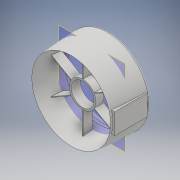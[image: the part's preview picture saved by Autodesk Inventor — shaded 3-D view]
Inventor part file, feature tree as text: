
AUTODESK INVENTOR PART (.ipt)
format: ipt  version: 2018 (Build 220112000, 112)  size: 280,064 bytes
history: native  units: mm
features: sketch x4, extrude x3, revolve x1, plane x1, fillet x1, projected_geometry x1
ambient origin geometry x8: Origin, YZ Plane, XZ Plane, XY Plane, X Axis, Y Axis, Z Axis, Center Point
bodies: Solid1 (feature_tree)
feature tree (11):
  revolve  "Revolution1"  Angle=90.0deg
  plane  "Work Plane1"
  extrude  "Extrusion2"  Depth=2.0mm TaperAngle=0.0deg
  extrude  "Extrusion3"  Depth=15.0mm TaperAngle=0.0deg
  extrude  "Extrusion4"  Depth=2.0mm
  fillet  "Fillet1"  [1 undecoded]
  sketch  "Sketch2"  dims[d0=37.25mm d2=90.0deg]
  sketch  "Sketch4"  dims[d3=24.2mm d4=2.0mm d14=10.0mm d15=0.0mm]
  projected_geometry  "Projected Loop1"
  sketch  "Sketch5"  dims[d16=22.0mm d17=15.0mm d18=20.0mm d19=0.0mm d20=0.0mm]
  sketch  "Sketch6"  dims[d21=15.0mm d22=0.0mm d23=2.0mm]
note: 1 required parameter value undecoded (feature->parameter linkage not recoverable at this tier; creation-order binding heuristic only, values carry confidence <= 0.55)
